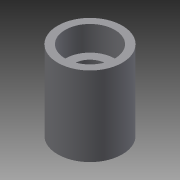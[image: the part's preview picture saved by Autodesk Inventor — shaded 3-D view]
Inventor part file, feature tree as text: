
AUTODESK INVENTOR PART (.ipt)
format: ipt  version: 2015 (Build 190159000, 159)  size: 84,480 bytes
history: native  units: in
note: dims shown in document units (in); Inventor stores cm internally (conversion verified against a paired STEP export)
features: extrude x2, sketch x1
ambient origin geometry x8: Origin, YZ Plane, XZ Plane, XY Plane, X Axis, Y Axis, Z Axis, Center Point
bodies: Body1 (feature_tree)
feature tree (3):
  sketch  "Sketch1"  dims[d0=0.3937in d1=0.5118in d4=0.2559in d11=0.1969in d12=0.0in d13=0.4331in d14=0.0in]
  extrude  "Extrusion5"  Depth=0.4331in
  extrude  "Extrusion6"  Depth=0.2559in
